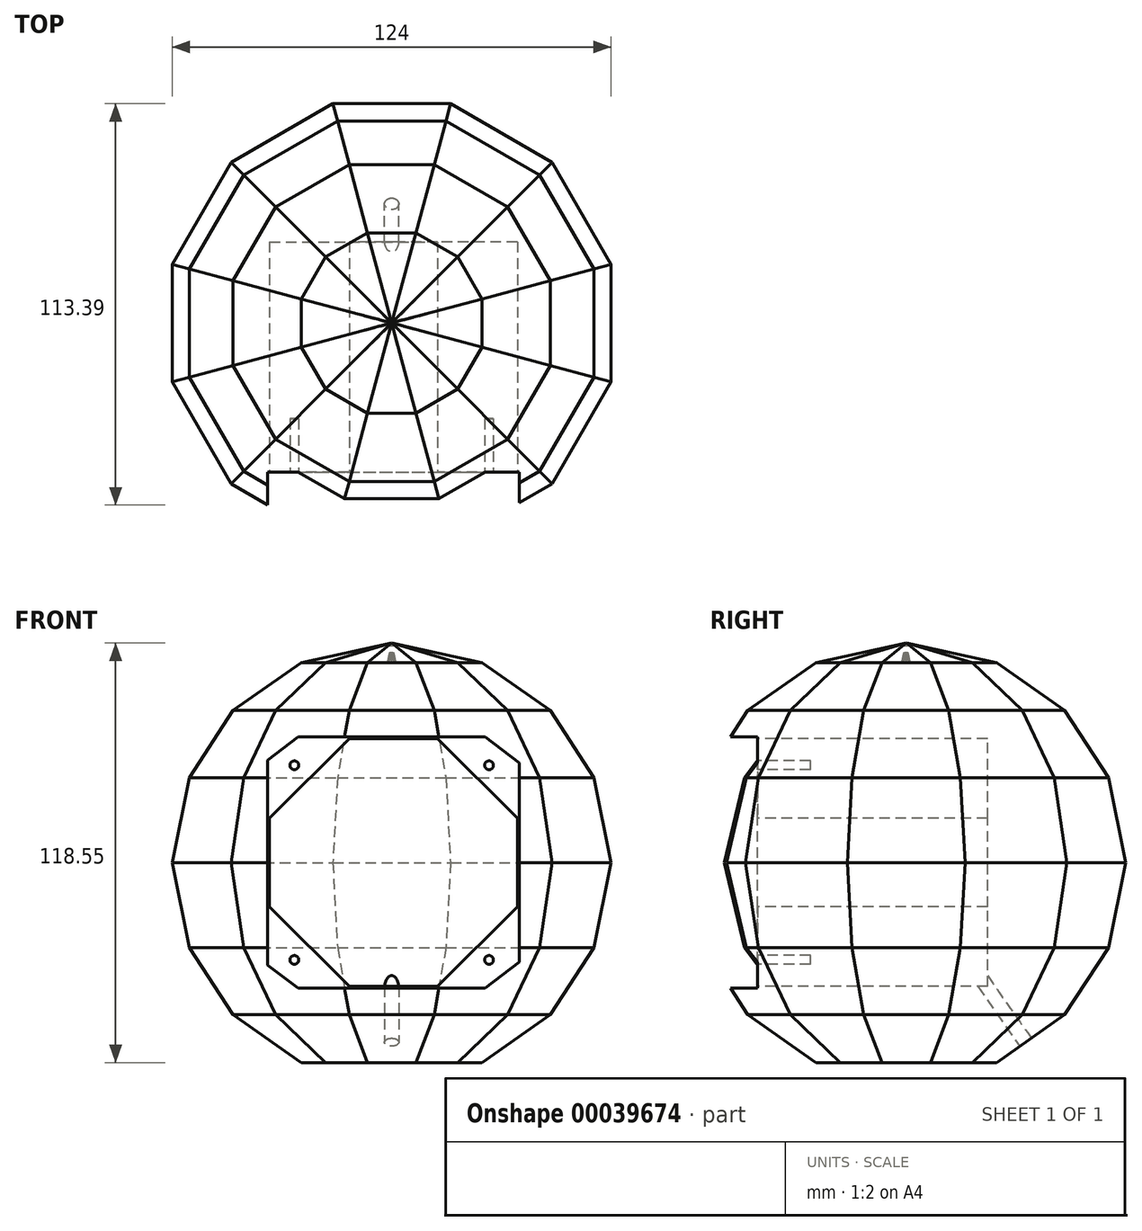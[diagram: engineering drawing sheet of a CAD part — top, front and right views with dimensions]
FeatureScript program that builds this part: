
annotation { "Feature Type Name" : "Feature", "Feature Type Description" : "" }
export const myFeature = defineFeature(function(context is Context, id is Id, definition is map)
    precondition{}
    {
        {
            var Q0;
            Q0=qCreatedBy(makeId("Front.planeOp"),FACE);
            var sketch = newSketch(context, id + "F0", { "sketchPlane" : qUnion([Q0])});
            skLineSegment(sketch, "E0", {"start": v(0, 0) * mm, "end": v(0, 113) * mm});
            skCircle(sketch, "E1", {"center": v(0, 56.5) * mm, "radius": 62.05 * mm});
            skSolve(sketch);
        }
        {
            var Q0;
            Q0=qCreatedBy(makeId("Top.planeOp"),FACE);
            var sketch = newSketch(context, id + "F1", { "sketchPlane" : qUnion([Q0])});
            skCircle(sketch, "E2.cCircle", {"center": v(0, 0) * mm, "radius": 25.5 * mm, "construction": true});
            skLineSegment(sketch, "E2.0", {"start": v(25.5, -6.83) * mm, "end": v(18.67, -18.67) * mm});
            skLineSegment(sketch, "E2.1", {"start": v(18.67, -18.67) * mm, "end": v(6.83, -25.5) * mm});
            skLineSegment(sketch, "E2.2", {"start": v(6.83, -25.5) * mm, "end": v(-6.83, -25.5) * mm});
            skLineSegment(sketch, "E2.3", {"start": v(-6.83, -25.5) * mm, "end": v(-18.67, -18.67) * mm});
            skLineSegment(sketch, "E2.4", {"start": v(-18.67, -18.67) * mm, "end": v(-25.5, -6.83) * mm});
            skLineSegment(sketch, "E2.5", {"start": v(-25.5, -6.83) * mm, "end": v(-25.5, 6.83) * mm});
            skLineSegment(sketch, "E2.6", {"start": v(-25.5, 6.83) * mm, "end": v(-18.67, 18.67) * mm});
            skLineSegment(sketch, "E2.7", {"start": v(-18.67, 18.67) * mm, "end": v(-6.83, 25.5) * mm});
            skLineSegment(sketch, "E2.8", {"start": v(-6.83, 25.5) * mm, "end": v(6.83, 25.5) * mm});
            skLineSegment(sketch, "E2.9", {"start": v(6.83, 25.5) * mm, "end": v(18.67, 18.67) * mm});
            skLineSegment(sketch, "E2.10", {"start": v(18.67, 18.67) * mm, "end": v(25.5, 6.83) * mm});
            skLineSegment(sketch, "E2.11", {"start": v(25.5, 6.83) * mm, "end": v(25.5, -6.83) * mm});
            skPoint(sketch, "E2.0.midPoint", {"position": v(22.08, -12.75) * mm});
            skSolve(sketch);
        }
        {
            var Q0;
            Q0 = qSketchRegion(id + "F1", true);
            extrude(context, id + "F2", {"entities" : qUnion([Q0]), "depth" : 13.5 * mm, "hasDraft" : true, "draftAngle" : 55 * degree});
        }
        {
            var Q0;
            Q0=makeQuery(id+"F2.opExtrude","CAP_FACE",FACE,{"disambiguationData":[OSD([sQuery(id+"F1.wireOp",EDGE,"E2.0"),sQuery(id+"F1.wireOp",EDGE,"E2.1"),sQuery(id+"F1.wireOp",EDGE,"E2.2"),sQuery(id+"F1.wireOp",EDGE,"E2.3"),sQuery(id+"F1.wireOp",EDGE,"E2.4"),sQuery(id+"F1.wireOp",EDGE,"E2.5"),sQuery(id+"F1.wireOp",EDGE,"E2.6"),sQuery(id+"F1.wireOp",EDGE,"E2.7"),sQuery(id+"F1.wireOp",EDGE,"E2.8"),sQuery(id+"F1.wireOp",EDGE,"E2.9"),sQuery(id+"F1.wireOp",EDGE,"E2.10"),sQuery(id+"F1.wireOp",EDGE,"E2.11")])],"isStart":false});
            var sketch = newSketch(context, id + "F3", { "sketchPlane" : qUnion([Q0])});
            skLineSegment(sketch, "E3.0", {"start": v(32.78, -32.78) * mm, "end": v(12, -44.78) * mm});
            skLineSegment(sketch, "E4.0", {"start": v(44.78, -12) * mm, "end": v(32.78, -32.78) * mm});
            skLineSegment(sketch, "E5.0", {"start": v(44.78, 12) * mm, "end": v(44.78, -12) * mm});
            skLineSegment(sketch, "E6.0", {"start": v(32.78, 32.78) * mm, "end": v(44.78, 12) * mm});
            skLineSegment(sketch, "E7.0", {"start": v(12, 44.78) * mm, "end": v(32.78, 32.78) * mm});
            skLineSegment(sketch, "E8.0", {"start": v(-12, 44.78) * mm, "end": v(12, 44.78) * mm});
            skLineSegment(sketch, "E9.0", {"start": v(-32.78, 32.78) * mm, "end": v(-12, 44.78) * mm});
            skLineSegment(sketch, "E10.0", {"start": v(-44.78, 12) * mm, "end": v(-32.78, 32.78) * mm});
            skLineSegment(sketch, "E11.0", {"start": v(-44.78, -12) * mm, "end": v(-44.78, 12) * mm});
            skLineSegment(sketch, "E12.0", {"start": v(-32.78, -32.78) * mm, "end": v(-44.78, -12) * mm});
            skLineSegment(sketch, "E13.0", {"start": v(-12, -44.78) * mm, "end": v(-32.78, -32.78) * mm});
            skLineSegment(sketch, "E14.0", {"start": v(12, -44.78) * mm, "end": v(-12, -44.78) * mm});
            skSolve(sketch);
        }
        {
            var Q0;
            Q0 = qSketchRegion(id + "F3", true);
            extrude(context, id + "F4", {"entities" : qUnion([Q0]), "operationType" : NewBodyOperationType.ADD, "depth" : 19 * mm, "hasDraft" : true, "draftAngle" : 33 * degree});
        }
        {
            var Q0;
            Q0=makeQuery(id+"F4.opExtrude","CAP_FACE",FACE,{"disambiguationData":[OSD([sQuery(id+"F3.wireOp",EDGE,"E3.0"),sQuery(id+"F3.wireOp",EDGE,"E4.0"),sQuery(id+"F3.wireOp",EDGE,"E5.0"),sQuery(id+"F3.wireOp",EDGE,"E6.0"),sQuery(id+"F3.wireOp",EDGE,"E7.0"),sQuery(id+"F3.wireOp",EDGE,"E8.0"),sQuery(id+"F3.wireOp",EDGE,"E9.0"),sQuery(id+"F3.wireOp",EDGE,"E10.0"),sQuery(id+"F3.wireOp",EDGE,"E11.0"),sQuery(id+"F3.wireOp",EDGE,"E12.0"),sQuery(id+"F3.wireOp",EDGE,"E13.0"),sQuery(id+"F3.wireOp",EDGE,"E14.0")])],"isStart":false});
            var sketch = newSketch(context, id + "F5", { "sketchPlane" : qUnion([Q0])});
            skLineSegment(sketch, "E15.0", {"start": v(41.81, -41.81) * mm, "end": v(15.3, -57.12) * mm});
            skLineSegment(sketch, "E16.0", {"start": v(57.12, -15.3) * mm, "end": v(41.81, -41.81) * mm});
            skLineSegment(sketch, "E17.0", {"start": v(57.12, 15.3) * mm, "end": v(57.12, -15.3) * mm});
            skLineSegment(sketch, "E18.0", {"start": v(41.81, 41.81) * mm, "end": v(57.12, 15.3) * mm});
            skLineSegment(sketch, "E19.0", {"start": v(15.3, 57.12) * mm, "end": v(41.81, 41.81) * mm});
            skLineSegment(sketch, "E20.0", {"start": v(-41.81, 41.81) * mm, "end": v(-15.3, 57.12) * mm});
            skLineSegment(sketch, "E21.0", {"start": v(-57.12, 15.3) * mm, "end": v(-41.81, 41.81) * mm});
            skLineSegment(sketch, "E22.0", {"start": v(-41.81, -41.81) * mm, "end": v(-57.12, -15.3) * mm});
            skLineSegment(sketch, "E23.0", {"start": v(-15.3, -57.12) * mm, "end": v(-41.81, -41.81) * mm});
            skLineSegment(sketch, "E24.0", {"start": v(15.3, -57.12) * mm, "end": v(-15.3, -57.12) * mm});
            skLineSegment(sketch, "E25.0", {"start": v(-57.12, -15.3) * mm, "end": v(-57.12, 15.3) * mm});
            skLineSegment(sketch, "E26.0", {"start": v(-15.3, 57.12) * mm, "end": v(15.3, 57.12) * mm});
            skSolve(sketch);
        }
        {
            var Q0;
            Q0 = qSketchRegion(id + "F5", true);
            extrude(context, id + "F6", {"entities" : qUnion([Q0]), "operationType" : NewBodyOperationType.ADD, "depth" : 24 * mm, "hasDraft" : true, "draftAngle" : 11.5 * degree});
        }
        {
            var Q0;
            Q0=makeQuery(id+"F6.opExtrude","CAP_FACE",FACE,{"disambiguationData":[OSD([sQuery(id+"F5.wireOp",EDGE,"E15.0"),sQuery(id+"F5.wireOp",EDGE,"E16.0"),sQuery(id+"F5.wireOp",EDGE,"E17.0"),sQuery(id+"F5.wireOp",EDGE,"E18.0"),sQuery(id+"F5.wireOp",EDGE,"E19.0"),sQuery(id+"F5.wireOp",EDGE,"E20.0"),sQuery(id+"F5.wireOp",EDGE,"E21.0"),sQuery(id+"F5.wireOp",EDGE,"E22.0"),sQuery(id+"F5.wireOp",EDGE,"E23.0"),sQuery(id+"F5.wireOp",EDGE,"E24.0"),sQuery(id+"F5.wireOp",EDGE,"E25.0"),sQuery(id+"F5.wireOp",EDGE,"E26.0")])],"isStart":false});
            var sketch = newSketch(context, id + "F7", { "sketchPlane" : qUnion([Q0])});
            skLineSegment(sketch, "E27.0", {"start": v(16.61, -62) * mm, "end": v(-16.61, -62) * mm});
            skLineSegment(sketch, "E28.0", {"start": v(-16.61, -62) * mm, "end": v(-45.39, -45.39) * mm});
            skLineSegment(sketch, "E29.0", {"start": v(-45.39, -45.39) * mm, "end": v(-62, -16.61) * mm});
            skLineSegment(sketch, "E30.0", {"start": v(45.39, -45.39) * mm, "end": v(16.61, -62) * mm});
            skLineSegment(sketch, "E31.0", {"start": v(62, -16.61) * mm, "end": v(45.39, -45.39) * mm});
            skLineSegment(sketch, "E32.0", {"start": v(62, 16.61) * mm, "end": v(62, -16.61) * mm});
            skLineSegment(sketch, "E33.0", {"start": v(45.39, 45.39) * mm, "end": v(62, 16.61) * mm});
            skLineSegment(sketch, "E34.0", {"start": v(16.61, 62) * mm, "end": v(45.39, 45.39) * mm});
            skLineSegment(sketch, "E35.0", {"start": v(-16.61, 62) * mm, "end": v(16.61, 62) * mm});
            skLineSegment(sketch, "E36.0", {"start": v(-45.39, 45.39) * mm, "end": v(-16.61, 62) * mm});
            skLineSegment(sketch, "E37.0", {"start": v(-62, 16.61) * mm, "end": v(-45.39, 45.39) * mm});
            skLineSegment(sketch, "E38.0", {"start": v(-62, -16.61) * mm, "end": v(-62, 16.61) * mm});
            skSolve(sketch);
        }
        {
            var Q0;
            Q0 = qSketchRegion(id + "F7", true);
            extrude(context, id + "F8", {"entities" : qUnion([Q0]), "operationType" : NewBodyOperationType.ADD, "depth" : 24 * mm, "hasDraft" : true, "draftAngle" : 11.5 * degree, "draftPullDirection" : true});
        }
        {
            var Q0;
            Q0=makeQuery(id+"F8.opExtrude","CAP_FACE",FACE,{"disambiguationData":[OSD([sQuery(id+"F7.wireOp",EDGE,"E27.0"),sQuery(id+"F7.wireOp",EDGE,"E28.0"),sQuery(id+"F7.wireOp",EDGE,"E29.0"),sQuery(id+"F7.wireOp",EDGE,"E30.0"),sQuery(id+"F7.wireOp",EDGE,"E31.0"),sQuery(id+"F7.wireOp",EDGE,"E32.0"),sQuery(id+"F7.wireOp",EDGE,"E33.0"),sQuery(id+"F7.wireOp",EDGE,"E34.0"),sQuery(id+"F7.wireOp",EDGE,"E35.0"),sQuery(id+"F7.wireOp",EDGE,"E36.0"),sQuery(id+"F7.wireOp",EDGE,"E37.0"),sQuery(id+"F7.wireOp",EDGE,"E38.0")])],"isStart":false});
            var sketch = newSketch(context, id + "F9", { "sketchPlane" : qUnion([Q0])});
            skLineSegment(sketch, "E39.0", {"start": v(41.81, -41.81) * mm, "end": v(15.3, -57.12) * mm});
            skLineSegment(sketch, "E40.0", {"start": v(57.12, -15.3) * mm, "end": v(41.81, -41.81) * mm});
            skLineSegment(sketch, "E41.0", {"start": v(15.3, -57.12) * mm, "end": v(-15.3, -57.12) * mm});
            skLineSegment(sketch, "E42.0", {"start": v(-15.3, -57.12) * mm, "end": v(-41.81, -41.81) * mm});
            skLineSegment(sketch, "E43.0", {"start": v(-41.81, -41.81) * mm, "end": v(-57.12, -15.3) * mm});
            skLineSegment(sketch, "E44.0", {"start": v(-57.12, -15.3) * mm, "end": v(-57.12, 15.3) * mm});
            skLineSegment(sketch, "E45.0", {"start": v(-57.12, 15.3) * mm, "end": v(-41.81, 41.81) * mm});
            skLineSegment(sketch, "E46.0", {"start": v(-41.81, 41.81) * mm, "end": v(-15.3, 57.12) * mm});
            skLineSegment(sketch, "E47.0", {"start": v(-15.3, 57.12) * mm, "end": v(15.3, 57.12) * mm});
            skLineSegment(sketch, "E48.0", {"start": v(15.3, 57.12) * mm, "end": v(41.81, 41.81) * mm});
            skLineSegment(sketch, "E49.0", {"start": v(41.81, 41.81) * mm, "end": v(57.12, 15.3) * mm});
            skLineSegment(sketch, "E50.0", {"start": v(57.12, 15.3) * mm, "end": v(57.12, -15.3) * mm});
            skSolve(sketch);
        }
        {
            var Q0;
            Q0 = qSketchRegion(id + "F9", true);
            extrude(context, id + "F10", {"entities" : qUnion([Q0]), "operationType" : NewBodyOperationType.ADD, "depth" : 19 * mm, "hasDraft" : true, "draftAngle" : 33 * degree, "draftPullDirection" : true});
        }
        {
            var Q0;
            Q0=makeQuery(id+"F10.opExtrude","CAP_FACE",FACE,{"disambiguationData":[OSD([sQuery(id+"F9.wireOp",EDGE,"E39.0"),sQuery(id+"F9.wireOp",EDGE,"E40.0"),sQuery(id+"F9.wireOp",EDGE,"E41.0"),sQuery(id+"F9.wireOp",EDGE,"E42.0"),sQuery(id+"F9.wireOp",EDGE,"E43.0"),sQuery(id+"F9.wireOp",EDGE,"E44.0"),sQuery(id+"F9.wireOp",EDGE,"E45.0"),sQuery(id+"F9.wireOp",EDGE,"E46.0"),sQuery(id+"F9.wireOp",EDGE,"E47.0"),sQuery(id+"F9.wireOp",EDGE,"E48.0"),sQuery(id+"F9.wireOp",EDGE,"E49.0"),sQuery(id+"F9.wireOp",EDGE,"E50.0")])],"isStart":false});
            var sketch = newSketch(context, id + "F11", { "sketchPlane" : qUnion([Q0])});
            skLineSegment(sketch, "E51.0", {"start": v(-12, -44.78) * mm, "end": v(-32.78, -32.78) * mm});
            skLineSegment(sketch, "E52.0", {"start": v(-32.78, -32.78) * mm, "end": v(-44.78, -12) * mm});
            skLineSegment(sketch, "E53.0", {"start": v(-44.78, -12) * mm, "end": v(-44.78, 12) * mm});
            skLineSegment(sketch, "E54.0", {"start": v(-44.78, 12) * mm, "end": v(-32.78, 32.78) * mm});
            skLineSegment(sketch, "E55.0", {"start": v(12, -44.78) * mm, "end": v(-12, -44.78) * mm});
            skLineSegment(sketch, "E56.0", {"start": v(32.78, -32.78) * mm, "end": v(12, -44.78) * mm});
            skLineSegment(sketch, "E57.0", {"start": v(44.78, -12) * mm, "end": v(32.78, -32.78) * mm});
            skLineSegment(sketch, "E58.0", {"start": v(44.78, 12) * mm, "end": v(44.78, -12) * mm});
            skLineSegment(sketch, "E59.0", {"start": v(32.78, 32.78) * mm, "end": v(44.78, 12) * mm});
            skLineSegment(sketch, "E60.0", {"start": v(12, 44.78) * mm, "end": v(32.78, 32.78) * mm});
            skLineSegment(sketch, "E61.0", {"start": v(-12, 44.78) * mm, "end": v(12, 44.78) * mm});
            skLineSegment(sketch, "E62.0", {"start": v(-32.78, 32.78) * mm, "end": v(-12, 44.78) * mm});
            skSolve(sketch);
        }
        {
            var Q0;
            Q0 = qSketchRegion(id + "F11", true);
            extrude(context, id + "F12", {"entities" : qUnion([Q0]), "operationType" : NewBodyOperationType.ADD, "depth" : 13.5 * mm, "hasDraft" : true, "draftAngle" : 55 * degree, "draftPullDirection" : true});
        }
        {
            var Q0;
            Q0=qCreatedBy(makeId("Front.planeOp"),FACE);
            cPlane(context, id + "F13", {"entities" : qUnion([Q0]), "cplaneType" : CPlaneType.OFFSET, "offset" : 62.05 * mm, "width" : 150 * mm, "height" : 150 * mm});
        }
        {
            var Q0;
            Q0=qCreatedBy(id+"F13.planeOp",FACE);
            var sketch = newSketch(context, id + "F14", { "sketchPlane" : qUnion([Q0])});
            skLineSegment(sketch, "E63.bottom", {"start": v(-35, 92) * mm, "end": v(36, 92) * mm});
            skLineSegment(sketch, "E63.top", {"start": v(-35, 21) * mm, "end": v(36, 21) * mm});
            skLineSegment(sketch, "E63.left", {"start": v(-35, 92) * mm, "end": v(-35, 21) * mm});
            skLineSegment(sketch, "E63.right", {"start": v(36, 92) * mm, "end": v(36, 21) * mm});
            skLineSegment(sketch, "E64", {"start": v(-35, 56.5) * mm, "end": v(36, 56.5) * mm, "construction": true});
            skLineSegment(sketch, "E65", {"start": v(0.5, 92) * mm, "end": v(0.5, 21) * mm, "construction": true});
            skSolve(sketch);
        }
        {
            var Q0;
            Q0 = qSketchRegion(id + "F14", true);
            extrude(context, id + "F15", {"entities" : qUnion([Q0]), "operationType" : NewBodyOperationType.REMOVE, "oppositeDirection" : true, "depth" : 20 * mm});
        }
        {
            var Q0;
            Q0=qCreatedBy(makeId("Front.planeOp"),FACE);
            var sketch = newSketch(context, id + "F16", { "sketchPlane" : qUnion([Q0])});
            skLineSegment(sketch, "E66", {"start": v(0, 56.62) * mm, "end": v(0, 118.55) * mm, "construction": true});
            skSolve(sketch);
        }
        {
            var Q0;
            Q0=sQuery(id+"F16.wireOp",VERTEX,"E66.end");
            var Q1;
            Q1=makeQuery(id+"F12.opExtrude","CAP_VERTEX",VERTEX,{"disambiguationData":[OSD([sQuery(id+"F11.wireOp",EDGE,"E55.0"),sQuery(id+"F11.wireOp",EDGE,"E56.0")])],"isStart":false});
            var Q2;
            Q2=makeQuery(id+"F12.opExtrude","CAP_VERTEX",VERTEX,{"disambiguationData":[OSD([sQuery(id+"F11.wireOp",EDGE,"E56.0"),sQuery(id+"F11.wireOp",EDGE,"E57.0")])],"isStart":false});
            cPlane(context, id + "F17", {"entities" : qUnion([Q0, Q1, Q2]), "cplaneType" : CPlaneType.THREE_POINT, "offset" : 150 * mm, "width" : 150 * mm, "height" : 150 * mm});
        }
        {
            var Q0;
            Q0=qCreatedBy(id+"F17.planeOp",FACE);
            var sketch = newSketch(context, id + "F18", { "sketchPlane" : qUnion([Q0])});
            skLineSegment(sketch, "E67", {"start": v(-5.52, 4.13) * mm, "end": v(-12.39, -21.96) * mm});
            skLineSegment(sketch, "E68", {"start": v(-12.39, -21.96) * mm, "end": v(6.39, -2.59) * mm});
            skLineSegment(sketch, "E69.0", {"start": v(6.39, -2.59) * mm, "end": v(-5.52, 4.13) * mm});
            skSolve(sketch);
        }
        {
            var Q0;
            Q0 = qSketchRegion(id + "F18", true);
            extrude(context, id + "F19", {"entities" : qUnion([Q0]), "endBound" : BoundingType.UP_TO_NEXT, "depth" : 25 * mm});
        }
        {
            var Q0;
            Q0=makeQuery(id+"F19.opExtrude","SWEPT_BODY",BODY,{"disambiguationData":[OSD([sQuery(id+"F18.wireOp",EDGE,"E67"),sQuery(id+"F18.wireOp",EDGE,"E68"),sQuery(id+"F18.wireOp",EDGE,"E69.0")])]});
            var Q1;
            Q1=sQuery(id+"F16.wireOp",EDGE,"E66");
            circularPattern(context, id + "F20", {"entities" : qUnion([Q0]), "axis" : qUnion([Q1]), "angle" : 30 * degree, "instanceCount" : 12});
        }
        {
            var Q0;
            Q0=makeQuery(id+"F15.boolean.opBoolean","COPY",FACE,{"derivedFrom":makeQuery(id+"F15.opExtrude","CAP_FACE",FACE,{"disambiguationData":[OSD([sQuery(id+"F14.wireOp",EDGE,"E63.bottom"),sQuery(id+"F14.wireOp",EDGE,"E63.top"),sQuery(id+"F14.wireOp",EDGE,"E63.left"),sQuery(id+"F14.wireOp",EDGE,"E63.right")])],"isStart":false})});
            var sketch = newSketch(context, id + "F21", { "sketchPlane" : qUnion([Q0])});
            skCircle(sketch, "E70", {"center": v(-27.5, 84) * mm, "radius": 1.25 * mm});
            skCircle(sketch, "E71", {"center": v(27.5, 84) * mm, "radius": 1.25 * mm});
            skCircle(sketch, "E72", {"center": v(-27.5, 29) * mm, "radius": 1.25 * mm});
            skCircle(sketch, "E73", {"center": v(27.5, 29) * mm, "radius": 1.25 * mm});
            skLineSegment(sketch, "E74", {"start": v(27.5, 84) * mm, "end": v(-27.5, 29) * mm, "construction": true});
            skPoint(sketch, "E75", {"position": v(0, 56.5) * mm});
            skSolve(sketch);
        }
        {
            var Q0;
            Q0 = qSketchRegion(id + "F21", true);
            extrude(context, id + "F22", {"entities" : qUnion([Q0]), "operationType" : NewBodyOperationType.REMOVE, "oppositeDirection" : true, "depth" : 15 * mm});
        }
        {
            var Q0;
            Q0=makeQuery(id+"F15.boolean.opBoolean","COPY",FACE,{"derivedFrom":makeQuery(id+"F15.opExtrude","CAP_FACE",FACE,{"disambiguationData":[OSD([sQuery(id+"F14.wireOp",EDGE,"E63.bottom"),sQuery(id+"F14.wireOp",EDGE,"E63.top"),sQuery(id+"F14.wireOp",EDGE,"E63.left"),sQuery(id+"F14.wireOp",EDGE,"E63.right")])],"isStart":false})});
            var sketch = newSketch(context, id + "F23", { "sketchPlane" : qUnion([Q0])});
            skLineSegment(sketch, "E76", {"start": v(-34.5, 69) * mm, "end": v(-12, 91.5) * mm});
            skLineSegment(sketch, "E77", {"start": v(-12, 91.5) * mm, "end": v(13, 91.5) * mm});
            skLineSegment(sketch, "E78", {"start": v(13, 91.5) * mm, "end": v(35.5, 69) * mm});
            skLineSegment(sketch, "E79", {"start": v(35.5, 69) * mm, "end": v(35.5, 44) * mm});
            skLineSegment(sketch, "E80", {"start": v(35.5, 44) * mm, "end": v(13, 21.5) * mm});
            skLineSegment(sketch, "E81", {"start": v(13, 21.5) * mm, "end": v(-12, 21.5) * mm});
            skLineSegment(sketch, "E82", {"start": v(-12, 21.5) * mm, "end": v(-34.5, 44) * mm});
            skLineSegment(sketch, "E83", {"start": v(-34.5, 44) * mm, "end": v(-34.5, 69) * mm});
            skLineSegment(sketch, "E84", {"start": v(0.5, 91.5) * mm, "end": v(0.5, 21.5) * mm, "construction": true});
            skLineSegment(sketch, "E85", {"start": v(35.5, 56.5) * mm, "end": v(-34.5, 56.5) * mm, "construction": true});
            skSolve(sketch);
        }
        {
            var Q0;
            Q0 = qSketchRegion(id + "F23", true);
            extrude(context, id + "F24", {"entities" : qUnion([Q0]), "operationType" : NewBodyOperationType.REMOVE, "oppositeDirection" : true, "depth" : 65 * mm});
        }
        {
            var Q0;
            Q0=makeQuery(id+"F2.opExtrude","SWEPT_FACE",FACE,{"disambiguationData":[OSD([sQuery(id+"F1.wireOp",EDGE,"E2.8")])]});
            var sketch = newSketch(context, id + "F25", { "sketchPlane" : qUnion([Q0])});
            skCircle(sketch, "E86", {"center": v(0, -30.89) * mm, "radius": 2 * mm});
            skSolve(sketch);
        }
        {
            var Q0;
            Q0 = qSketchRegion(id + "F25", true);
            extrude(context, id + "F26", {"entities" : qUnion([Q0]), "operationType" : NewBodyOperationType.REMOVE, "oppositeDirection" : true, "depth" : 25 * mm});
        }
    });
